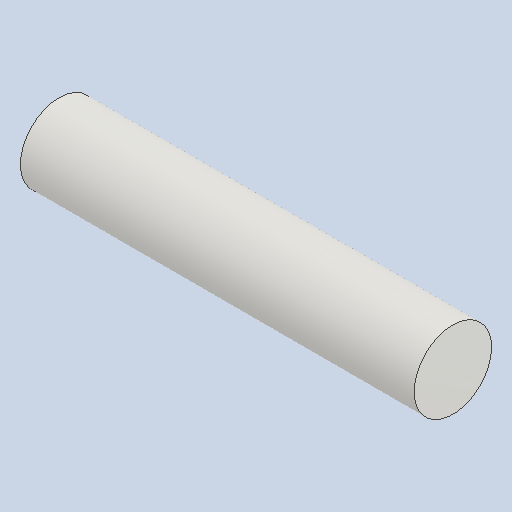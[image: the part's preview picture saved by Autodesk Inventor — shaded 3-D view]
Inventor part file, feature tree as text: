
AUTODESK INVENTOR PART (.ipt)
format: ipt  version: 2024 (Build 280153000, 153)  size: 86,016 bytes
history: native  units: in
note: dims shown in document units (in); Inventor stores cm internally (conversion verified against a paired STEP export)
features: other x3, revolve x1
ambient origin geometry x6: Origin, XZ Plane, XY Plane, X Axis, Y Axis, Z Axis
bodies: Solid1 (feature_tree)
feature tree (4):
  revolve  "Revolution1"  [1 undecoded]
  other  "Start Plane"
  other  "Origin point"
  other  "Main Sketch"
note: 1 required parameter value undecoded (feature->parameter linkage not recoverable at this tier; creation-order binding heuristic only, values carry confidence <= 0.55)
